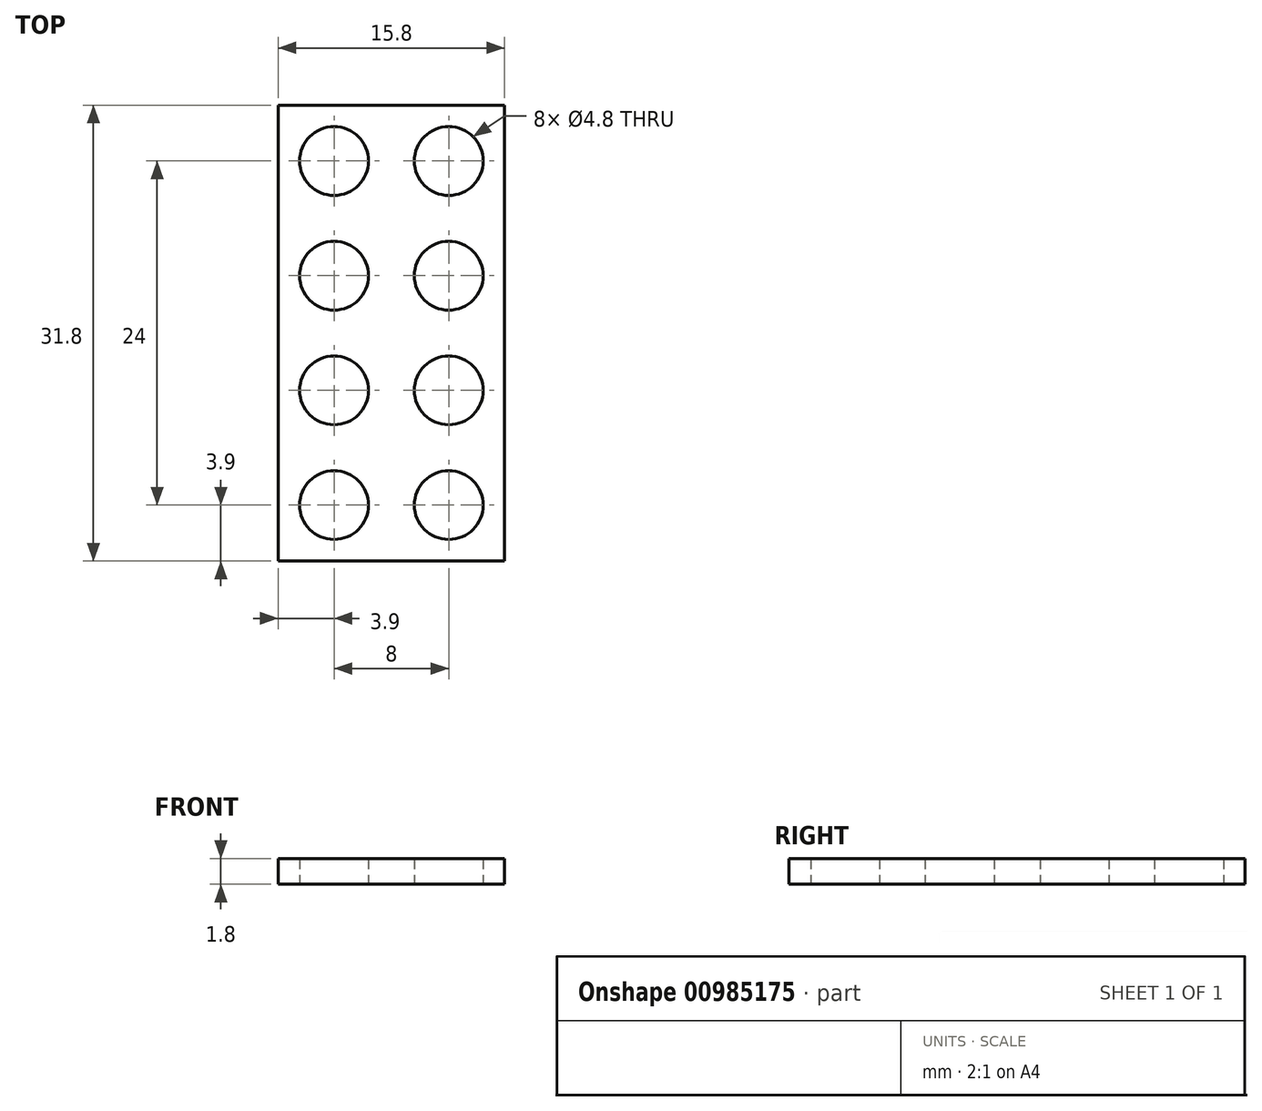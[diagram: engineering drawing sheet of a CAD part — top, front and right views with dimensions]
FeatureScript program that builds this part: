
annotation { "Feature Type Name" : "Feature", "Feature Type Description" : "" }
export const myFeature = defineFeature(function(context is Context, id is Id, definition is map)
    precondition{}
    {
        {
            var Q0;
            Q0=qCreatedBy(makeId("Top.planeOp"),FACE);
            var sketch = newSketch(context, id + "F0", { "sketchPlane" : qUnion([Q0])});
            skLineSegment(sketch, "E0.bottom", {"start": v(7.9, -15.9) * mm, "end": v(-7.9, -15.9) * mm});
            skLineSegment(sketch, "E0.top", {"start": v(7.9, 15.9) * mm, "end": v(-7.9, 15.9) * mm});
            skLineSegment(sketch, "E0.left", {"start": v(7.9, -15.9) * mm, "end": v(7.9, 15.9) * mm});
            skLineSegment(sketch, "E0.right", {"start": v(-7.9, -15.9) * mm, "end": v(-7.9, 15.9) * mm});
            skPoint(sketch, "E0.middle", {"position": v(0, 0) * mm});
            skCircle(sketch, "E1", {"center": v(-4, 12) * mm, "radius": 2.4 * mm});
            skCircle(sketch, "E2.1.0.0", {"center": v(4, 12) * mm, "radius": 2.4 * mm});
            skLineSegment(sketch, "E2.direction1", {"start": v(-4, 12) * mm, "end": v(4, 12) * mm, "construction": true});
            skCircle(sketch, "E3.1.0.0", {"center": v(-4, 4) * mm, "radius": 2.4 * mm});
            skCircle(sketch, "E3.1.0.1", {"center": v(4, 4) * mm, "radius": 2.4 * mm});
            skCircle(sketch, "E3.2.0.0", {"center": v(-4, -4) * mm, "radius": 2.4 * mm});
            skCircle(sketch, "E3.2.0.1", {"center": v(4, -4) * mm, "radius": 2.4 * mm});
            skCircle(sketch, "E3.3.0.0", {"center": v(-4, -12) * mm, "radius": 2.4 * mm});
            skCircle(sketch, "E3.3.0.1", {"center": v(4, -12) * mm, "radius": 2.4 * mm});
            skLineSegment(sketch, "E3.direction1", {"start": v(-4, 12) * mm, "end": v(-4, 4) * mm, "construction": true});
            skLineSegment(sketch, "E4", {"start": v(0, 22.1) * mm, "end": v(0, -22.1) * mm, "construction": true});
            skLineSegment(sketch, "E5", {"start": v(-20.22, 0) * mm, "end": v(20.22, 0) * mm, "construction": true});
            skSolve(sketch);
        }
        {
            var Q0;
            Q0 = qSketchRegion(id + "F0", true);
            extrude(context, id + "F1", {"entities" : qUnion([Q0]), "depth" : 1.8 * mm, "offsetDistance" : 25.4 * mm});
        }
    });
